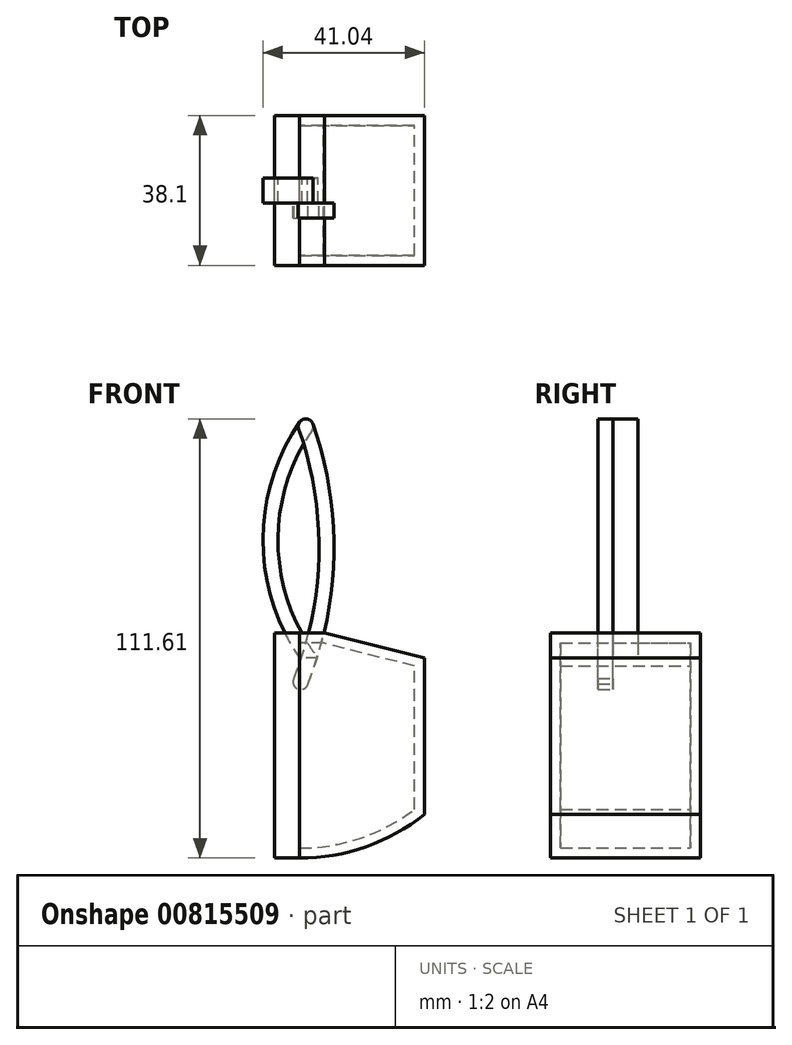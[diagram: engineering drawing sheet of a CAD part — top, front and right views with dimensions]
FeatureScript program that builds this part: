
annotation { "Feature Type Name" : "Feature", "Feature Type Description" : "" }
export const myFeature = defineFeature(function(context is Context, id is Id, definition is map)
    precondition{}
    {
        {
            var Q0;
            Q0=qCreatedBy(makeId("Front.planeOp"),FACE);
            var sketch = newSketch(context, id + "F0", { "sketchPlane" : qUnion([Q0])});
            skLineSegment(sketch, "E0", {"start": v(0, 0) * mm, "end": v(0, -50.8) * mm});
            skArc(sketch, "E1", {"start": v(0, -50.8) * mm, "mid": v(16.82, -47.93) * mm, "end": v(31.75, -39.66) * mm});
            skLineSegment(sketch, "E2", {"start": v(31.75, -39.66) * mm, "end": v(31.75, 0) * mm});
            skLineSegment(sketch, "E3", {"start": v(31.75, 0) * mm, "end": v(6.35, 6.35) * mm});
            skLineSegment(sketch, "E4", {"start": v(6.35, 6.35) * mm, "end": v(0, 6.35) * mm});
            skLineSegment(sketch, "E5", {"start": v(0, 6.35) * mm, "end": v(0, 0) * mm});
            skSolve(sketch);
        }
        {
            var Q0;
            Q0 = qSketchRegion(id + "F0", true);
            extrude(context, id + "F1", {"entities" : qUnion([Q0]), "endBound" : BoundingType.SYMMETRIC, "depth" : 38.1 * mm, "offsetDistance" : 25.4 * mm});
        }
        {
            var Q0;
            Q0=makeQuery(id+"F1.opExtrude","SWEPT_FACE",FACE,{"disambiguationData":[OSD([sQuery(id+"F0.wireOp",EDGE,"E0"),sQuery(id+"F0.wireOp",EDGE,"E5")])]});
            shell(context, id + "F2", {"entities" : qUnion([Q0]), "thickness" : 2.54 * mm});
        }
        {
            var Q0;
            Q0=qCreatedBy(makeId("Front.planeOp"),FACE);
            var sketch = newSketch(context, id + "F3", { "sketchPlane" : qUnion([Q0])});
            skArc(sketch, "E6", {"start": v(0, 59.98) * mm, "mid": v(-9.29, 29.99) * mm, "end": v(0, 0) * mm});
            skArc(sketch, "E7.0", {"start": v(3.14, 57.82) * mm, "mid": v(-5.46, 28.66) * mm, "end": v(4.7, 0) * mm});
            skArc(sketch, "E8", {"start": v(3.14, 57.82) * mm, "mid": v(2.65, 60.47) * mm, "end": v(0, 59.98) * mm});
            skLineSegment(sketch, "E9", {"start": v(4.7, 0) * mm, "end": v(0, 0) * mm});
            skSolve(sketch);
        }
        {
            var Q0;
            Q0 = qSketchRegion(id + "F3", true);
            extrude(context, id + "F4", {"entities" : qUnion([Q0]), "operationType" : NewBodyOperationType.ADD, "endBound" : BoundingType.SYMMETRIC, "depth" : 6.35 * mm, "offsetDistance" : 25.4 * mm});
        }
        {
            var Q0;
            Q0=qCreatedBy(makeId("Front.planeOp"),FACE);
            var sketch = newSketch(context, id + "F5", { "sketchPlane" : qUnion([Q0])});
            skLineSegment(sketch, "E10", {"start": v(0, -50.8) * mm, "end": v(-6.35, -50.8) * mm});
            skLineSegment(sketch, "E11", {"start": v(-6.35, -50.8) * mm, "end": v(-6.35, 0) * mm});
            skLineSegment(sketch, "E12", {"start": v(-6.35, 0) * mm, "end": v(-6.35, 6.35) * mm});
            skLineSegment(sketch, "E13", {"start": v(-6.35, 6.35) * mm, "end": v(0, 6.35) * mm});
            skLineSegment(sketch, "E14", {"start": v(0, 6.35) * mm, "end": v(0, -50.8) * mm});
            skSolve(sketch);
        }
        {
            var Q0;
            Q0 = qSketchRegion(id + "F5", true);
            extrude(context, id + "F6", {"entities" : qUnion([Q0]), "endBound" : BoundingType.SYMMETRIC, "depth" : 38.1 * mm, "offsetDistance" : 25.4 * mm});
        }
        {
            var Q0;
            Q0=makeQuery(id+"F4.opExtrude","CAP_FACE",FACE,{"disambiguationData":[OSD([sQuery(id+"F3.wireOp",EDGE,"E6"),sQuery(id+"F3.wireOp",EDGE,"E7.0"),sQuery(id+"F3.wireOp",EDGE,"E8"),sQuery(id+"F3.wireOp",EDGE,"E9")])],"isStart":false});
            var sketch = newSketch(context, id + "F7", { "sketchPlane" : qUnion([Q0])});
            skCircle(sketch, "E15", {"center": v(1.57, 58.9) * mm, "radius": 1.9 * mm, "construction": true});
            skArc(sketch, "E16", {"start": v(2.13, -6.52) * mm, "mid": v(8.74, 26.4) * mm, "end": v(3.37, 59.54) * mm});
            skArc(sketch, "E17.0", {"start": v(-1.4, -5.12) * mm, "mid": v(4.93, 26.47) * mm, "end": v(-0.22, 58.27) * mm});
            skArc(sketch, "E18", {"start": v(3.37, 59.54) * mm, "mid": v(0.94, 60.7) * mm, "end": v(-0.22, 58.27) * mm});
            skArc(sketch, "E19", {"start": v(-1.4, -5.12) * mm, "mid": v(-0.44, -7.85) * mm, "end": v(2.13, -6.52) * mm});
            skSolve(sketch);
        }
        {
            var Q0;
            Q0 = qSketchRegion(id + "F7", true);
            extrude(context, id + "F8", {"entities" : qUnion([Q0]), "depth" : 3.8 * mm, "offsetDistance" : 25.4 * mm});
        }
    });
